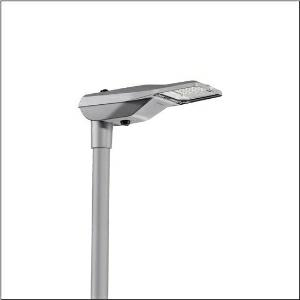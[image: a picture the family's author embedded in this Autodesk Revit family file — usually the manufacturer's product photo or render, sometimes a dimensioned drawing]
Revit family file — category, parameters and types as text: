
# Revit family: streetlight_sl_21_iq_micro___st1_0a_5xe1d21y08db_e1fc
name_source: partatom
category: Lighting Fixtures
units: mm (PartAtom-declared; Revit-internal decimal feet)

## family parameters
Cut with Voids When Loaded = No
Host = Face
Light Source = No
Part Type = Normal
Room Calculation Point = No
Round Connector Dimension = Use Diameter
Shared = No

## types (1)
- --- (1 x LED, 4100 lm, 39.1 W, 2200K)
    Apparent Load = 39 VA
    CIE Flux Codes = 37 72 97 100 100
    Color Rendering = 70
    Color Temperature = 2200K
    Default Elevation = 1800 mm
    Description = Streetlight SL 21 iQ micro, mast luminaire, primary light control with lens, of PMMA, primary optical cover: cover, of toughened safety glass, transparent, light distribution: ST1.0a, light emission: direct distribution, primary light characteristic: asymmetric, installation type: post-top, side-entry, LED, High Power LED, rated luminous flux: 4.100lm, luminous efficacy: 105lm/W, light colour: 722, colour temperature: 2200K, control gear: iQ-Street Remote, D4i with power reduction, control: pre-setting: logarithmic dimming characteristic, Street-Remote, Auto-Match, Temp-Guard, Lumen-Switch, Night-Set, Smart-Wire, Light-Fading, Desk-Remote (wireless, voltage-free reading and setting of iQ features in the workshop via application-optimized NFC function/RFID function), optimised constant luminous flux control (CLO 2.0), mains connection: 220..240V, AC, 50/60Hz, start of lifetime: 39W, end of service life: 41W, reduction: 17W, luminaire housing, of diecast aluminium, powder-coated, SITECO metallic grey (DB 702S), corrosivity category C5 high according to DIN EN ISO 12944, please order mast flange separately, inclination adjustable: 0°, 5°, 10°, 15°, sealing non-destructively replaceable, multi-level sealing system, length: 528mm, width: 235mm, height: 110mm, mast flange for spigot size: 42mm (side-entry): 5XC10008XM4, 60/48mm (side-entry/post-top): 5XC10108XM2, 76/60mm (side-entry/post-top): 5XC10108XM1, mounting height: 4..8m, Smart Interface below and above, protection rating (complete): IP66, insulation class (complete): insulation class II (safety insulation), certification: CE, ENEC, ENEC+, VDE, impact resistance: IK10, permissible operating ambient temperature for outdoor applications: -40..+50°C, standard-compliant lighting for roads and squares, packaging unit: 1 piece

Light Distribution: ST1.0a
    Height = 110 mm
    Lamp = 1 x LED
    Lamp Light Flux = 4100 lm
    Lamp Power = 39.1 W
    Lamp count = 1
    Length = 528 mm
    Luminous efficacy = 105 lm/W
    Manufacturer = Siteco
    ModVariant = No
    Model = 5XE1D21Y08DB
    Number of Poles = 1
    OnlyDefault = Yes
    Power Factor = 1
    Product Name = Streetlight SL 21 iQ micro | ST1.0a
    Product group = mast luminaire | pylon top
    ProductGroupID = 6100
    Protection Class = Protection class II
    Protection Degree = IP 66
    RLX_Detail_Level = 1
    RLX_Emergency_Light_Flux = 0 lm
    RLX_Emergency_Type = 0
    RLX_Emergency_Type_DB = No
    RlxData = <blob elided: 98933 chars, md5=b55cd00b>
    Socket = socket
    Standby Power = 0 W
    System Light Flux = 4100 lm
    System Power = 39 W
    Type Comments = factory setting: luminous flux: 100 % | dim-lin: 254 | 765 mA
    Type Image = l_1007239.jpg
    URL = http://relux.com
    VarID = @adj_115693
    Voltage = 0 V
    Weight = 0.00 kg
    Width = 235 mm

## geometry (parser evidence)
native form markers: Blend x4, Sweep x10
no freeform markers — native parametric forms only
